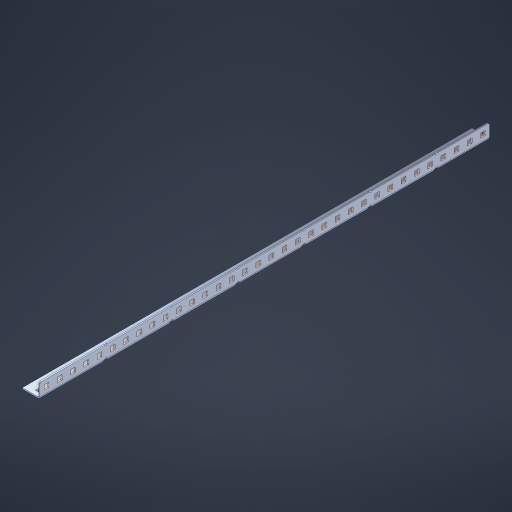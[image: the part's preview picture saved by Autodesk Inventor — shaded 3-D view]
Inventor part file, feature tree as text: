
AUTODESK INVENTOR PART (.ipt)
format: ipt  version: 2023 (Build 270158000, 158)  size: 1,028,608 bytes
history: native  units: in
note: dims shown in document units (in); Inventor stores cm internally (conversion verified against a paired STEP export)
features: other x73, extrude x67, sheet_metal_op x10, sketch x8, mirror x1, pattern_linear x1, chamfer x1
ambient origin geometry x8: Origin, YZ Plane, XZ Plane, XY Plane, X Axis, Y Axis, Z Axis, Center Point
bodies: Solid1 (feature_tree), Body (feature_tree)
feature tree (161):
  other  "Flange Pattern Plane"
  sheet_metal_op  "Flange Pattern"
  sheet_metal_op  "Body Pattern"
  other  "Arc Length"
  mirror  "Notch Mirror"
  pattern_linear  "Notch Pattern"  Spacing1=0.1875in  [1 undecoded]
  chamfer  "End Chamfer"
  extrude  "Half Cut"  Depth=0.0469in
  sketch  "Sketch1"  dims[d0=2.5in]
  other  "Plate1"
  sketch  "Sketch2"  dims[d1=17.0in]
  other  "Plate2"
  sheet_metal_op  "Bend1"
  sheet_metal_op  "Corner1"
  sketch  "Sketch3"  dims[d2=0.0469in]
  other  "Flange Pattern Sketch"
  sketch  "Sketch7"  dims[d3=0.0469in]
  other  "Srf1"
  other  "Srf2"
  sketch  "Sketch8"  dims[d4=0.0234in]
  sketch  "Sketch9"  dims[d5=0.0938in]
  other  "Srf91"
  sheet_metal_op  "Body Pattern Sketch"
  other  "Srf92"
  sketch  "Sketch13"  dims[d6=0.0469in]
  sketch  "Sketch14"  dims[d7=0.5in d8=90.0deg d9=0.0312in d10=0.1875in d11=0.0469in d12=0.0469in d16=0.182in d17=0.02in d18=0.0469in d19=0.0in d20=0.25in d21=0.25in d46=0.172in d47=1.0in d48=0.0in d49=0.182in d50=0.02in d51=0.25in d52=0.25in d53=0.0469in d54=0.0in d55=0.172in d56=1.0in d57=0.0in d60=13.3858in d62=0.5in d63=0.3937in d65=0.5in d85=0.1227in d86=0.1659in d88=0.04in d89=0.0469in d90=0.0in d91=0.04in d92=0.0491in d95=2.5in d96=0.04in d97=0.25in d98=45.0deg d101=0.0in d102=2.497in d131=0.5in d132=13.3858in d134=0.5in d139=0.5in]
  other  "Srf856"
  other  "Srf1310"
  other  "Srf1311"
  other  "Srf1312"
  other  "Srf1376"
  other  "Srf1377"
  other  "Srf1728"
  other  "Srf1755"
  other  "Srf1878"
  other  "Srf1879"
  other  "Srf1880"
  other  "Srf1881"
  other  "Srf1882"
  other  "Srf1883"
  other  "Srf1884"
  other  "Srf1885"
  other  "Srf1886"
  other  "Srf1887"
  other  "Srf1888"
  other  "Srf1889"
  other  "Srf1890"
  other  "Srf1891"
  other  "Srf1892"
  other  "Srf1893"
  other  "Srf1894"
  other  "Srf1895"
  other  "Srf1896"
  other  "Srf1897"
  other  "Srf1898"
  other  "Srf1899"
  other  "Srf1900"
  other  "Srf1901"
  other  "Srf1902"
  other  "Srf1903"
  other  "Srf1904"
  other  "Srf1905"
  other  "Srf1942"
  other  "Srf1943"
  other  "Srf1944"
  other  "Srf1945"
  other  "Srf1946"
  other  "Srf1947"
  other  "Srf1948"
  other  "Srf1949"
  other  "Srf1950"
  other  "Srf1951"
  other  "Srf1952"
  other  "Srf1953"
  other  "Srf1954"
  other  "Srf1955"
  other  "Srf1956"
  other  "Srf1957"
  other  "Srf1958"
  other  "Srf1959"
  other  "Srf1960"
  other  "Srf1961"
  other  "Srf1962"
  other  "Srf1963"
  other  "Srf1964"
  other  "Srf1965"
  other  "Srf1966"
  other  "Srf1967"
  other  "Srf1968"
  other  "Srf1969"
  sheet_metal_op  "Flange Stamp"
  sheet_metal_op  "Flange Circle"
  sheet_metal_op  "Body Stamp"
  sheet_metal_op  "Body Circle"
  sheet_metal_op  "Notch"
  extrude  "ExtrusionSrf2"  Depth=0.0469in
  extrude  "ExtrusionSrf92"  Depth=0.5in
  extrude  "ExtrusionSrf856"  Depth=0.02in
  extrude  "ExtrusionSrf1310"  Depth=0.0469in
  extrude  "ExtrusionSrf1311"  TaperAngle=0.0deg  [1 undecoded]
  extrude  "ExtrusionSrf1312"  Depth=0.5in
  extrude  "ExtrusionSrf1376"  Depth=0.5in
  extrude  "ExtrusionSrf1377"  Depth=0.5in
  extrude  "ExtrusionSrf1728"  Depth=0.5in TaperAngle=0.0deg
  extrude  "ExtrusionSrf1755"  Depth=0.5in
  extrude  "ExtrusionSrf1878"  Depth=0.02in
  extrude  "ExtrusionSrf1879"  Depth=0.5in
  extrude  "ExtrusionSrf1880"  Depth=0.5in
  extrude  "ExtrusionSrf1881"  Depth=0.0469in
  extrude  "ExtrusionSrf1882"  TaperAngle=0.0deg  [1 undecoded]
  extrude  "ExtrusionSrf1883"  Depth=0.5in
  extrude  "ExtrusionSrf1884"  Depth=0.5in TaperAngle=0.0deg
  extrude  "ExtrusionSrf1885"  Depth=0.5in
  extrude  "ExtrusionSrf1886"  Depth=0.5in
  extrude  "ExtrusionSrf1887"  Depth=0.5in
  extrude  "ExtrusionSrf1888"  Depth=0.5in
  extrude  "ExtrusionSrf1889"  Depth=0.5in
  extrude  "ExtrusionSrf1890"  Depth=0.0469in
  extrude  "ExtrusionSrf1891"  TaperAngle=0.0deg  [1 undecoded]
  extrude  "ExtrusionSrf1892"  Depth=0.5in
  extrude  "ExtrusionSrf1893"  Depth=0.5in
  extrude  "ExtrusionSrf1894"  Depth=0.5in
  extrude  "ExtrusionSrf1895"  Depth=0.5in TaperAngle=45.0deg
  extrude  "ExtrusionSrf1896"  TaperAngle=0.0deg  [1 undecoded]
  extrude  "ExtrusionSrf1897"  Depth=0.5in
  extrude  "ExtrusionSrf1898"  Depth=0.5in
  extrude  "ExtrusionSrf1899"  Depth=0.5in
  extrude  "ExtrusionSrf1900"  Depth=0.5in
  extrude  "ExtrusionSrf1901"  Depth=0.5in
  extrude  "ExtrusionSrf1902"  [1 undecoded]
  extrude  "ExtrusionSrf1903"  [1 undecoded]
  extrude  "ExtrusionSrf1904"  [1 undecoded]
  extrude  "ExtrusionSrf1905"  [1 undecoded]
  extrude  "ExtrusionSrf1942"  [1 undecoded]
  extrude  "ExtrusionSrf1943"  [1 undecoded]
  extrude  "ExtrusionSrf1944"  [1 undecoded]
  extrude  "ExtrusionSrf1945"  [1 undecoded]
  extrude  "ExtrusionSrf1946"  [1 undecoded]
  extrude  "ExtrusionSrf1947"  [1 undecoded]
  extrude  "ExtrusionSrf1948"  [1 undecoded]
  extrude  "ExtrusionSrf1949"  [1 undecoded]
  extrude  "ExtrusionSrf1950"  [1 undecoded]
  extrude  "ExtrusionSrf1951"  [1 undecoded]
  extrude  "ExtrusionSrf1952"  [1 undecoded]
  extrude  "ExtrusionSrf1953"  [1 undecoded]
  extrude  "ExtrusionSrf1954"  [1 undecoded]
  extrude  "ExtrusionSrf1955"  [1 undecoded]
  extrude  "ExtrusionSrf1956"  [1 undecoded]
  extrude  "ExtrusionSrf1957"  [1 undecoded]
  extrude  "ExtrusionSrf1958"  [1 undecoded]
  extrude  "ExtrusionSrf1959"  [1 undecoded]
  extrude  "ExtrusionSrf1960"  [1 undecoded]
  extrude  "ExtrusionSrf1961"  [1 undecoded]
  extrude  "ExtrusionSrf1962"  [1 undecoded]
  extrude  "ExtrusionSrf1963"  [1 undecoded]
  extrude  "ExtrusionSrf1964"  [1 undecoded]
  extrude  "ExtrusionSrf1965"  [1 undecoded]
  extrude  "ExtrusionSrf1966"  [1 undecoded]
  extrude  "ExtrusionSrf1967"  [1 undecoded]
  extrude  "ExtrusionSrf1968"  [1 undecoded]
  extrude  "ExtrusionSrf1969"  [1 undecoded]
note: 37 required parameter values undecoded (feature->parameter linkage not recoverable at this tier; creation-order binding heuristic only, values carry confidence <= 0.55)
